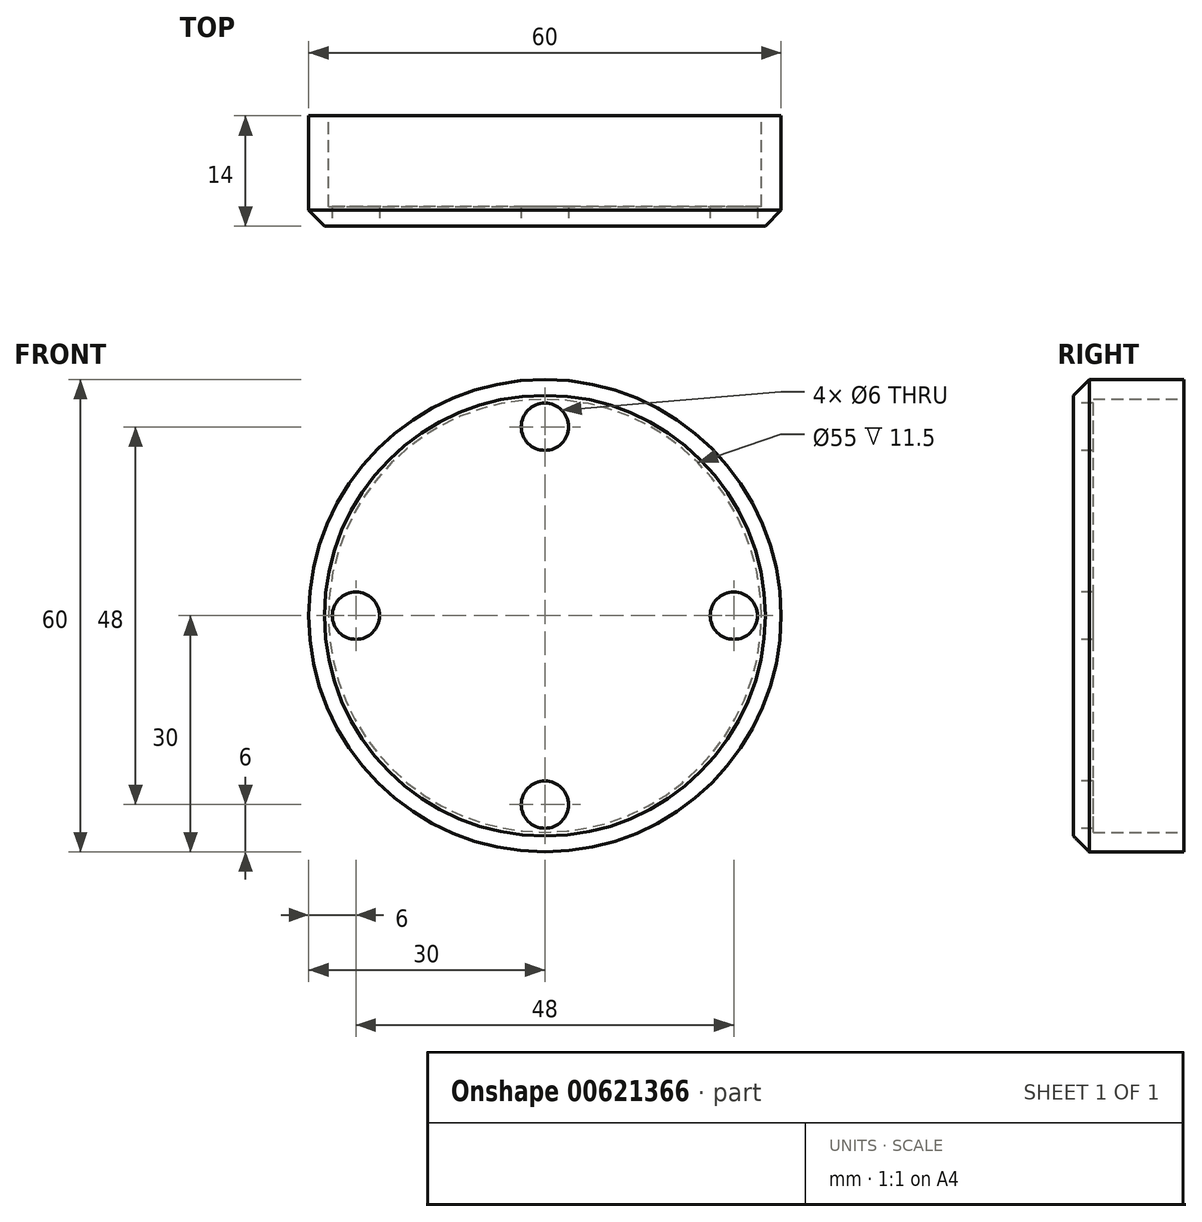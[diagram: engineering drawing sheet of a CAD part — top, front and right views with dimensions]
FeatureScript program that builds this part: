
annotation { "Feature Type Name" : "Feature", "Feature Type Description" : "" }
export const myFeature = defineFeature(function(context is Context, id is Id, definition is map)
    precondition{}
    {
        {
            var Q0;
            Q0=qCreatedBy(makeId("Front.planeOp"),FACE);
            var sketch = newSketch(context, id + "F0", { "sketchPlane" : qUnion([Q0])});
            skCircle(sketch, "E0", {"center": v(0, 0) * mm, "radius": 30 * mm});
            skSolve(sketch);
        }
        {
            var Q0;
            Q0 = qSketchRegion(id + "F0", true);
            extrude(context, id + "F1", {"entities" : qUnion([Q0]), "depth" : 14 * mm, "offsetDistance" : 25 * mm});
        }
        {
            var Q0;
            Q0=makeQuery(id+"F1.opExtrude","CAP_FACE",FACE,{"disambiguationData":[OSD([sQuery(id+"F0.wireOp",EDGE,"E0")])],"isStart":true});
            shell(context, id + "F2", {"entities" : qUnion([Q0]), "thickness" : 2.5 * mm});
        }
        {
            var Q0;
            Q0=makeQuery(id+"F1.opExtrude","CAP_FACE",FACE,{"disambiguationData":[OSD([sQuery(id+"F0.wireOp",EDGE,"E0")])],"isStart":false});
            var sketch = newSketch(context, id + "F3", { "sketchPlane" : qUnion([Q0])});
            skCircle(sketch, "E1", {"center": v(0, 0) * mm, "radius": 24 * mm, "construction": true});
            skCircle(sketch, "E2", {"center": v(0, -24) * mm, "radius": 3 * mm});
            skCircle(sketch, "E3", {"center": v(-24, 0) * mm, "radius": 3 * mm});
            skCircle(sketch, "E4", {"center": v(24, 0) * mm, "radius": 3 * mm});
            skCircle(sketch, "E5", {"center": v(0, 24) * mm, "radius": 3 * mm});
            skSolve(sketch);
        }
        {
            var Q0;
            Q0 = qSketchRegion(id + "F3", true);
            extrude(context, id + "F4", {"entities" : qUnion([Q0]), "operationType" : NewBodyOperationType.REMOVE, "endBound" : BoundingType.UP_TO_NEXT, "oppositeDirection" : true, "depth" : 25 * mm, "offsetDistance" : 25 * mm});
        }
        {
            var Q0;
            Q0=makeQuery(id+"F1.opExtrude","CAP_EDGE",EDGE,{"disambiguationData":[OSD([sQuery(id+"F0.wireOp",EDGE,"E0")])],"isStart":false});
            chamfer(context, id + "F5", {"entities" : qUnion([Q0]), "width" : 2 * mm, "tangentPropagation" : true});
        }
    });
